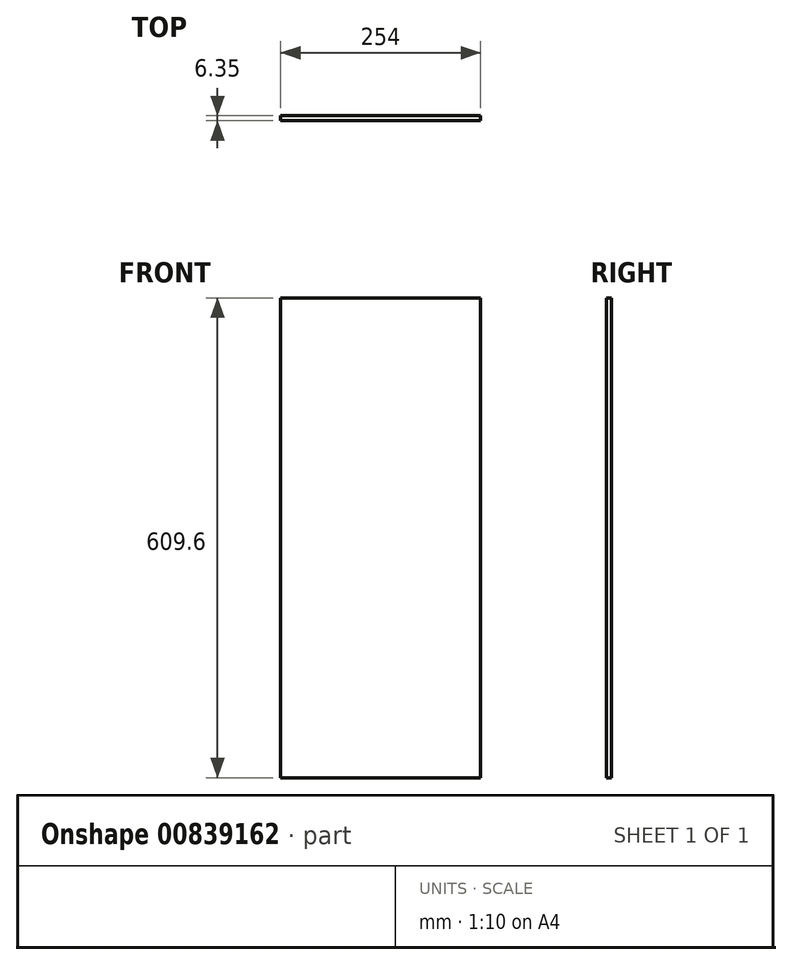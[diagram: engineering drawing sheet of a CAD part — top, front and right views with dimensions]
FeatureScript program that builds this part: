
annotation { "Feature Type Name" : "Feature", "Feature Type Description" : "" }
export const myFeature = defineFeature(function(context is Context, id is Id, definition is map)
    precondition{}
    {
        {
            var Q0;
            Q0=qCreatedBy(makeId("Front.planeOp"),FACE);
            var sketch = newSketch(context, id + "F0", { "sketchPlane" : qUnion([Q0])});
            skLineSegment(sketch, "E0.bottom", {"start": v(0, 0) * mm, "end": v(-254, 0) * mm});
            skLineSegment(sketch, "E0.top", {"start": v(0, 609.6) * mm, "end": v(-254, 609.6) * mm});
            skLineSegment(sketch, "E0.left", {"start": v(0, 0) * mm, "end": v(0, 609.6) * mm});
            skLineSegment(sketch, "E0.right", {"start": v(-254, 0) * mm, "end": v(-254, 609.6) * mm});
            skSolve(sketch);
        }
        {
            var Q0;
            Q0=qSketchRegion(id+"F0",true);
            extrude(context, id + "F1", {"entities" : qUnion([Q0]), "oppositeDirection" : true, "depth" : 6.35 * mm, "offsetDistance" : 25.4 * mm});
        }
    });
